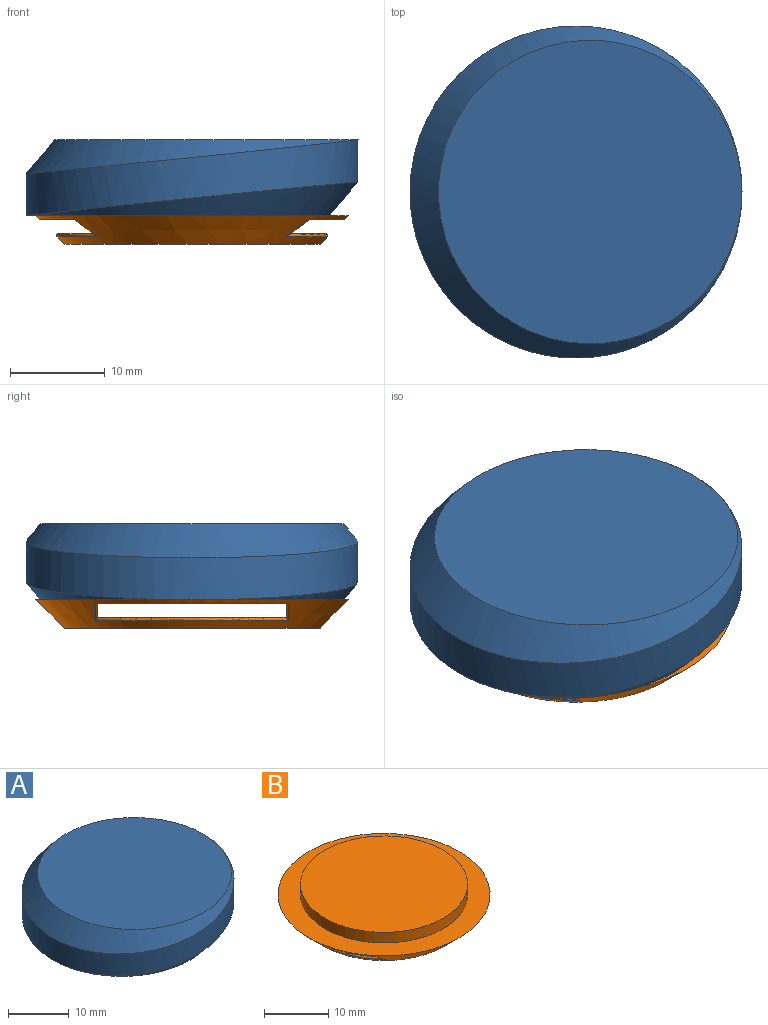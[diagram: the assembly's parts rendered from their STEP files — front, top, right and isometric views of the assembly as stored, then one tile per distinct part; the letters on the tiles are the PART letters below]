
ASSEMBLY  parts=2 mates=1
PART A: 9 faces, bbox 41x38x8 mm
  f0: cylinder r=17.5mm len=35mm, axis (0,0,-1), area 478mm2, adj f1,f3
  f1: cone r=10.13mm half-angle=40deg, axis (0,0,-1), area 245.6mm2, adj f0,f2
  f2: plane 32x32mm, normal (0,0,1), area 804.2mm2, adj f1
  f3: cone r=8.32mm half-angle=40deg, axis (0,0,1), area 245.4mm2, adj f0,f4
  f4: plane 32x32mm, normal (0,0,-1), area 252.7mm2, adj f3,f5
  f5: cylinder r=13.25mm len=26.5mm, axis (0,0,-1), area 291.4mm2, adj f4,f6
  f6: plane 26.5x26.5mm, normal (0,0,-1), area 60.7mm2, adj f5,f8
  f7: plane 25x25mm, normal (0,0,-1), area 490.9mm2, adj f8
  f8: cylinder r=12.5mm len=25mm, axis (0,0,-1), area 117.8mm2, adj f6,f7
PART B: 15 faces, bbox 33.2x33.2x5.2 mm
  f0: cone r=13.5mm half-angle=45deg, axis (0,0,1), area 281.4mm2, adj f1,f2,f5,f9,f10,f11,f12,f13
  f1: plane 27x27mm, normal (0,0,-1), area 572.6mm2, adj f0
  f2: plane 33x33mm, normal (0,0,1), area 324.4mm2, adj f0,f3
  f3: cylinder r=13mm len=26mm, axis (0,0,-1), area 163.4mm2, adj f2,f4
  f4: plane 26x26mm, normal (0,0,1), area 530.9mm2, adj f3
  f5: plane 32.39x20.77mm, normal (0,0,-1), area 599.9mm2, adj f0,f6,f8,f9,f11,f12,f14
  f6: plane 24.18x1.51mm, normal (0,1,0), area 33.2mm2, adj f5,f7,f10,f11,f13,f14
  f7: plane 28.23x20mm, normal (0,0,1), area 513mm2, adj f6,f8,f10,f13
  f8: plane 24.18x1.51mm, normal (0,-1,0), area 33.2mm2, adj f5,f7,f9,f10,f12,f13
  f9: bspline ~5.63x4.36mm, area 1.2mm2, adj f0,f5,f8,f10
  f10: torus R=14.12mm, axis (0,0,-1), area 10.6mm2, adj f0,f6,f7,f8,f9,f11
  f11: bspline ~5.63x4.36mm, area 1.2mm2, adj f0,f5,f6,f10
  f12: bspline ~5.63x4.36mm, area 1.2mm2, adj f0,f5,f8,f13
  f13: torus R=14.12mm, axis (0,0,-1), area 10.6mm2, adj f0,f6,f7,f8,f12,f14
  f14: bspline ~5.63x4.36mm, area 1.2mm2, adj f0,f5,f6,f13
PLACE A t=(-0.02,-0.04,-4.05)mm fixed
PLACE B t=(-0.02,-0.04,-7.05)mm
MATE fastened B.f3 <-> A.f5  axis (0,0,1) through (-0.02,-0.04,-4.05)mm
